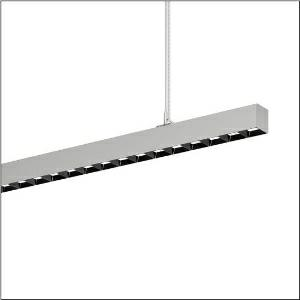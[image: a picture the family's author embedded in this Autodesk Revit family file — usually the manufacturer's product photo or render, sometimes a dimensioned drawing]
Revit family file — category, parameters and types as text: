
# Revit family: silica_r__21_51mx34dc4dsb_5451
name_source: partatom
category: Lighting Fixtures
units: mm (PartAtom-declared; Revit-internal decimal feet)

## family parameters
Cut with Voids When Loaded = No
Host = Face
Light Source = No
Part Type = Normal
Room Calculation Point = No
Round Connector Dimension = Use Diameter
Shared = No

## types (1)
- --- (1 x LED, 19200 lm, 120.3 W, 4000K)
    Apparent Load = 120 VA
    CIE Flux Codes = 74 94 99 56 100
    Color Rendering = 80
    Color Temperature = 4000K
    Default Elevation = 1800 mm
    Description = Silica® 21, office luminaire, primary light control with darklight reflector, of PMMA, black, light emission: direct/indirect distribution, primary light characteristic: asymmetric, installation type: suspended mounting, LED, rated luminous flux: 19.200lm, luminous efficacy: 160lm/W, light colour: 840, colour temperature: 4000K, with terminal, 3+2-pole, max. 2.5mm², mains connection: 220..240V, AC, 50/60Hz, rated input power: 120.3W, luminaire housing, of aluminium, metallic grey (RAL 9006), length: 3.004mm, width: 53mm, height: 53mm, protection rating (complete): IP20, insulation class (complete): insulation class I (protective earthing), certification: CE, permissible operating ambient temperature: 0..+35°C, standard: EN 50419, packaging unit: 1 piece
    Height = 53 mm
    Lamp = 1 x LED
    Lamp Light Flux = 19200 lm
    Lamp Power = 120.3 W
    Lamp count = 1
    Length = 3004 mm
    Luminous efficacy = 160 lm/W
    Manufacturer = Siteco
    ModVariant = No
    Model = 51MX34DC4DSB
    Mounting Place = Ceiling
    Mounting Type = Pendant
    Number of Poles = 1
    OnlyDefault = Yes
    Power Factor = 1
    Product Name = Silica® 21
    Product group = office luminaire | ceiling pendant
    ProductGroupID = 905
    Protection Class = Protection class I
    Protection Degree = IP 20
    RLX_Detail_Level = 1
    RlxData = <blob elided: 67673 chars, md5=a243766e>
    Socket = socket
    Standby Power = 0 W
    System Light Flux = 19200 lm
    System Power = 120 W
    Type Comments = factory setting: luminous flux: 100 % | dim-lin: 254 | 418 mA
    Type Image = l_1251731.jpg
    URL = http://relux.com
    VarID = @adj_028943
    Voltage = 0 V
    Weight = 0.00 kg
    Width = 53 mm

## geometry (parser evidence)
native form markers: Blend x4, Sweep x11
no freeform markers — native parametric forms only
